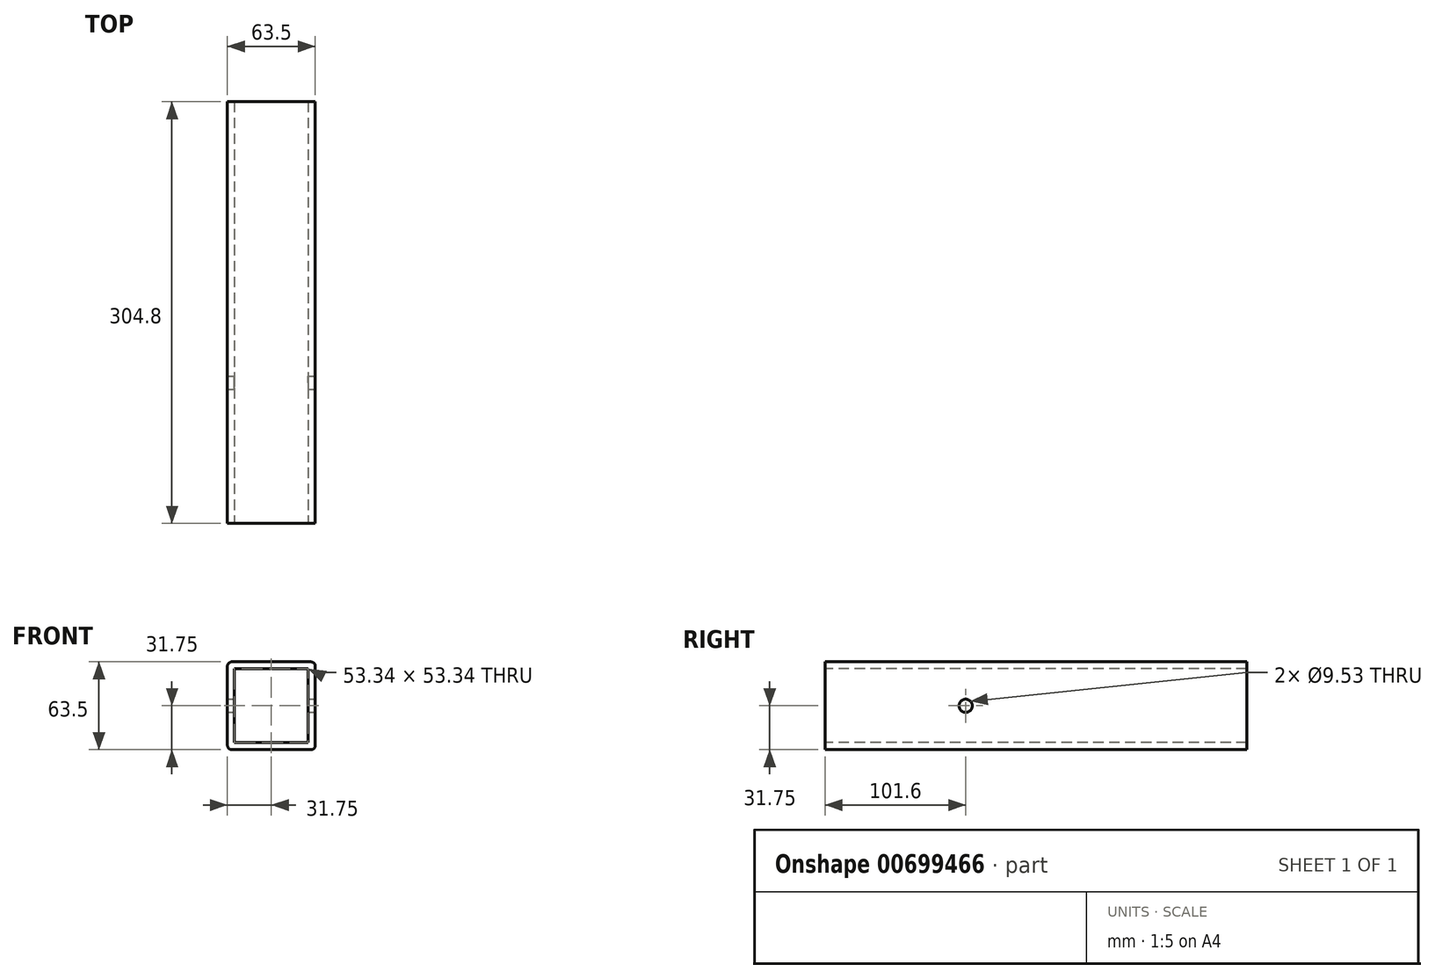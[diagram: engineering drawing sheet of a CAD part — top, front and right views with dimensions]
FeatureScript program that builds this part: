
annotation { "Feature Type Name" : "Feature", "Feature Type Description" : "" }
export const myFeature = defineFeature(function(context is Context, id is Id, definition is map)
    precondition{}
    {
        {
            var Q0;
            Q0=qCreatedBy(makeId("Front.planeOp"),FACE);
            var sketch = newSketch(context, id + "F0", { "sketchPlane" : qUnion([Q0])});
            skLineSegment(sketch, "E0.bottom", {"start": v(28.57, 31.75) * mm, "end": v(-28.58, 31.75) * mm});
            skLineSegment(sketch, "E0.top", {"start": v(28.58, -31.75) * mm, "end": v(-28.57, -31.75) * mm});
            skLineSegment(sketch, "E0.left", {"start": v(31.75, 28.58) * mm, "end": v(31.75, -28.57) * mm});
            skLineSegment(sketch, "E0.right", {"start": v(-31.75, 28.57) * mm, "end": v(-31.75, -28.58) * mm});
            skPoint(sketch, "E0.middle", {"position": v(0, 0) * mm});
            skPoint(sketch, "E1.visualSharp", {"position": v(-31.75, 31.75) * mm});
            skArc(sketch, "E1.filletArc", {"start": v(-28.58, 31.75) * mm, "mid": v(-30.82, 30.82) * mm, "end": v(-31.75, 28.57) * mm});
            skPoint(sketch, "E2.visualSharp", {"position": v(-31.75, -31.75) * mm});
            skArc(sketch, "E2.filletArc", {"start": v(-31.75, -28.57) * mm, "mid": v(-30.82, -30.82) * mm, "end": v(-28.57, -31.75) * mm});
            skPoint(sketch, "E3.visualSharp", {"position": v(31.75, -31.75) * mm});
            skArc(sketch, "E3.filletArc", {"start": v(28.58, -31.75) * mm, "mid": v(30.82, -30.82) * mm, "end": v(31.75, -28.57) * mm});
            skPoint(sketch, "E4.visualSharp", {"position": v(31.75, 31.75) * mm});
            skArc(sketch, "E4.filletArc", {"start": v(31.75, 28.57) * mm, "mid": v(30.82, 30.82) * mm, "end": v(28.57, 31.75) * mm});
            skLineSegment(sketch, "E5.0", {"start": v(26.67, 26.67) * mm, "end": v(-26.67, 26.67) * mm});
            skLineSegment(sketch, "E5.1", {"start": v(26.67, 26.67) * mm, "end": v(26.67, -26.67) * mm});
            skLineSegment(sketch, "E5.2", {"start": v(26.67, -26.67) * mm, "end": v(-26.67, -26.67) * mm});
            skLineSegment(sketch, "E5.3", {"start": v(-26.67, 26.67) * mm, "end": v(-26.67, -26.67) * mm});
            skSolve(sketch);
        }
        {
            var Q0;
            Q0 = qSketchRegion(id + "F0", true);
            extrude(context, id + "F1", {"entities" : qUnion([Q0]), "oppositeDirection" : true, "depth" : 304.8 * mm, "offsetDistance" : 25.4 * mm});
        }
        {
            var Q0;
            Q0=makeQuery(id+"F1.opExtrude","SWEPT_FACE",FACE,{"disambiguationData":[OSD([sQuery(id+"F0.wireOp",EDGE,"E0.left")])]});
            var sketch = newSketch(context, id + "F2", { "sketchPlane" : qUnion([Q0])});
            skPoint(sketch, "E6", {"position": v(101.6, 0) * mm});
            skSolve(sketch);
        }
        {
            var Q0;
            Q0=sQuery(id+"F2.wireOp",VERTEX,"E6");
            var Q1;
            Q1=makeQuery(id+"F1.opExtrude","SWEPT_BODY",BODY,{"disambiguationData":[OSD([sQuery(id+"F0.wireOp",EDGE,"E0.bottom"),sQuery(id+"F0.wireOp",EDGE,"E0.top"),sQuery(id+"F0.wireOp",EDGE,"E0.left"),sQuery(id+"F0.wireOp",EDGE,"E0.right"),sQuery(id+"F0.wireOp",EDGE,"E1.filletArc"),sQuery(id+"F0.wireOp",EDGE,"E2.filletArc"),sQuery(id+"F0.wireOp",EDGE,"E3.filletArc"),sQuery(id+"F0.wireOp",EDGE,"E4.filletArc"),sQuery(id+"F0.wireOp",EDGE,"E5.0"),sQuery(id+"F0.wireOp",EDGE,"E5.1"),sQuery(id+"F0.wireOp",EDGE,"E5.2"),sQuery(id+"F0.wireOp",EDGE,"E5.3")])]});
            hole(context, id + "F3", {"style" : HoleStyle.SIMPLE, "endStyle" : HoleEndStyle.THROUGH, "holeDiameter" : 9.52 * mm, "majorDiameter" : 6.35 * mm, "isTappedThrough" : true, "tappedDepth" : 12.7 * mm, "tapClearance" : 3, "locations" : qUnion([Q0]), "scope" : qUnion([Q1])});
        }
    });
